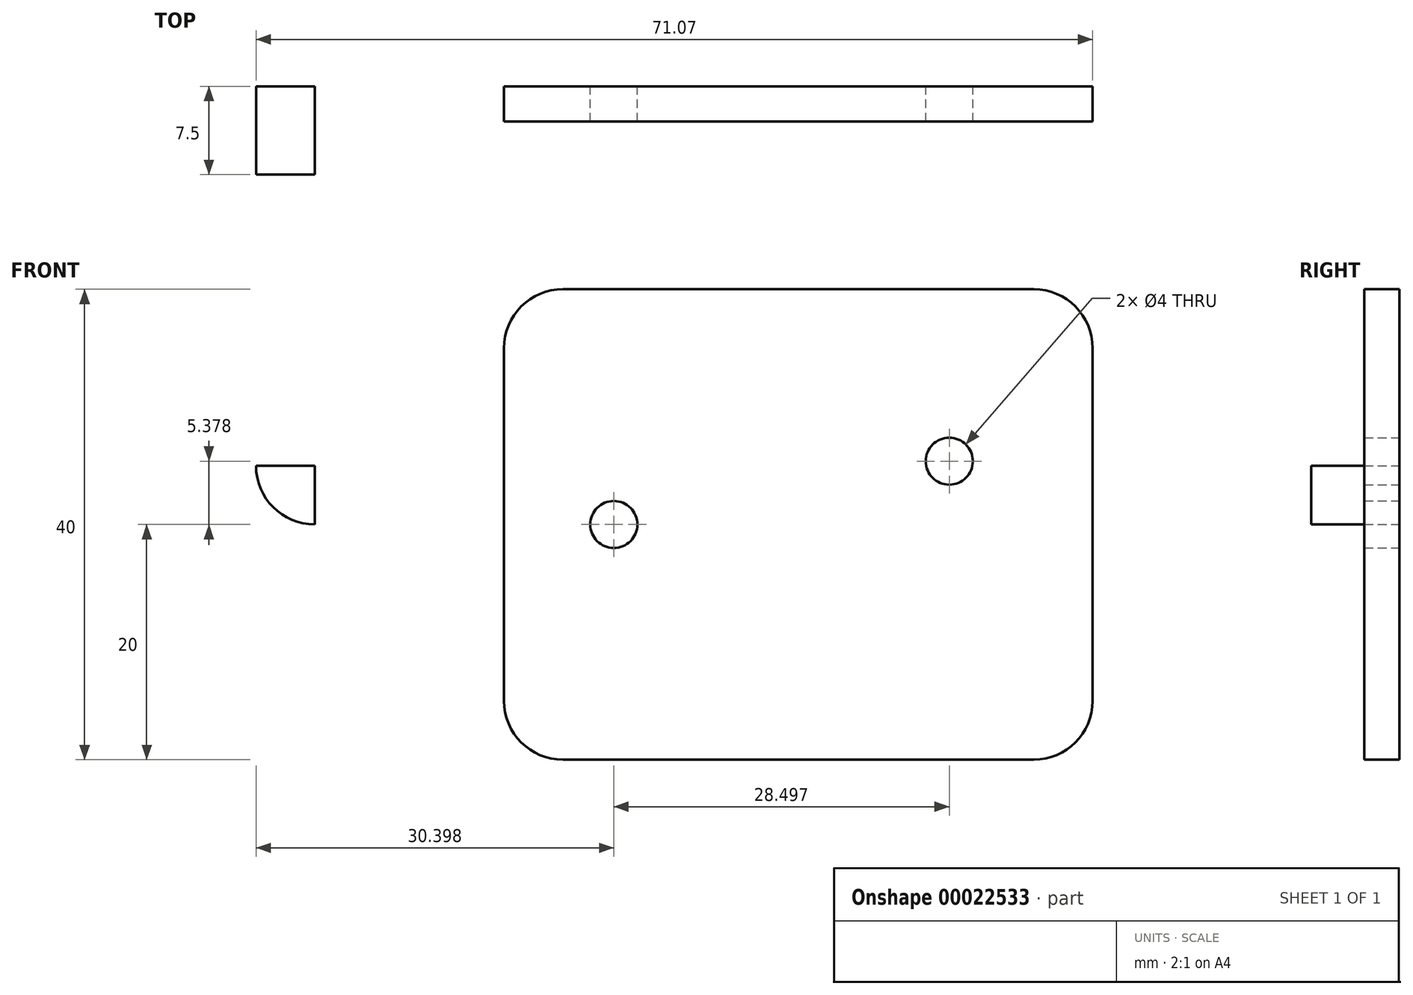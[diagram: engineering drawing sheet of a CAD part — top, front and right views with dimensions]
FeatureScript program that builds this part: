
annotation { "Feature Type Name" : "Feature", "Feature Type Description" : "" }
export const myFeature = defineFeature(function(context is Context, id is Id, definition is map)
    precondition{}
    {
        {
            var Q0;
            Q0=qCreatedBy(makeId("Front.planeOp"),FACE);
            var sketch = newSketch(context, id + "F0", { "sketchPlane" : qUnion([Q0])});
            skPoint(sketch, "E0.rect.middle", {"position": v(0, 0) * mm});
            skLineSegment(sketch, "E1.rect.bottom", {"start": v(20, 20) * mm, "end": v(-20, 20) * mm});
            skLineSegment(sketch, "E1.rect.top", {"start": v(20, -20) * mm, "end": v(-20, -20) * mm});
            skLineSegment(sketch, "E1.rect.left", {"start": v(25, 15) * mm, "end": v(25, -15) * mm});
            skLineSegment(sketch, "E1.rect.right", {"start": v(-25, 15) * mm, "end": v(-25, -15) * mm});
            skCircle(sketch, "E2", {"center": v(-15.67, 0) * mm, "radius": 2 * mm});
            skCircle(sketch, "E3", {"center": v(12.82, 5.38) * mm, "radius": 2 * mm});
            skPoint(sketch, "E4.visualSharp", {"position": v(-25, 20) * mm});
            skArc(sketch, "E4.filletArc", {"start": v(-20, 20) * mm, "mid": v(-23.54, 18.54) * mm, "end": v(-25, 15) * mm});
            skPoint(sketch, "E5.visualSharp", {"position": v(25, 20) * mm});
            skArc(sketch, "E5.filletArc", {"start": v(25, 15) * mm, "mid": v(23.54, 18.54) * mm, "end": v(20, 20) * mm});
            skPoint(sketch, "E6.visualSharp", {"position": v(25, -20) * mm});
            skArc(sketch, "E6.filletArc", {"start": v(20, -20) * mm, "mid": v(23.54, -18.54) * mm, "end": v(25, -15) * mm});
            skPoint(sketch, "E7.visualSharp", {"position": v(-25, -20) * mm});
            skArc(sketch, "E7.filletArc", {"start": v(-25, -15) * mm, "mid": v(-23.54, -18.54) * mm, "end": v(-20, -20) * mm});
            skLineSegment(sketch, "E8", {"start": v(-15.67, 0) * mm, "end": v(12.82, 5.38) * mm});
            skSolve(sketch);
        }
        {
            var Q0;
            Q0=makeQuery(id+"F0.imprint","IMPRINT",FACE,{"disambiguationData":[TD([[makeQuery(id+"F0.imprint","IMPRINT",EDGE,{"derivedFrom":sQuery(id+"F0.wireOp",EDGE,"E1.rect.bottom")}),1.0]])]});
            var Q1;
            Q1=makeQuery(id+"F0.imprint","IMPRINT",FACE,{"disambiguationData":[TD([[makeQuery(id+"F0.imprint","IMPRINT",EDGE,{"derivedFrom":sQuery(id+"F0.wireOp",EDGE,"b02cd445-e791-4f87-9c50-e9e083848f1d.rect.bottom")}),1.0]])]});
            extrude(context, id + "F1", {"entities" : qUnion([Q0, Q1]), "depth" : 3 * mm});
        }
        {
            var Q0;
            Q0=qCreatedBy(makeId("Front.planeOp"),FACE);
            var sketch = newSketch(context, id + "F2", { "sketchPlane" : qUnion([Q0])});
            skLineSegment(sketch, "E9.bottom", {"start": v(-41.07, 0) * mm, "end": v(-41.07, 0) * mm});
            skLineSegment(sketch, "E9.top", {"start": v(-46.07, 5) * mm, "end": v(-41.07, 5) * mm});
            skLineSegment(sketch, "E9.left", {"start": v(-46.07, 5) * mm, "end": v(-46.07, 5) * mm});
            skLineSegment(sketch, "E9.right", {"start": v(-41.07, 0) * mm, "end": v(-41.07, 5) * mm});
            skPoint(sketch, "E10.visualSharp", {"position": v(-46.07, 0) * mm});
            skArc(sketch, "E10.filletArc", {"start": v(-46.07, 5) * mm, "mid": v(-44.6, 1.46) * mm, "end": v(-41.07, 0) * mm});
            skSolve(sketch);
        }
        {
            var Q0;
            Q0=makeQuery(id+"F2.imprint","IMPRINT",FACE,{"disambiguationData":[TD([[makeQuery(id+"F2.imprint","IMPRINT",EDGE,{"derivedFrom":sQuery(id+"F2.wireOp",EDGE,"E9.top")}),-1.0]])]});
            extrude(context, id + "F3", {"entities" : qUnion([Q0]), "depth" : 7.5 * mm});
        }
    });
